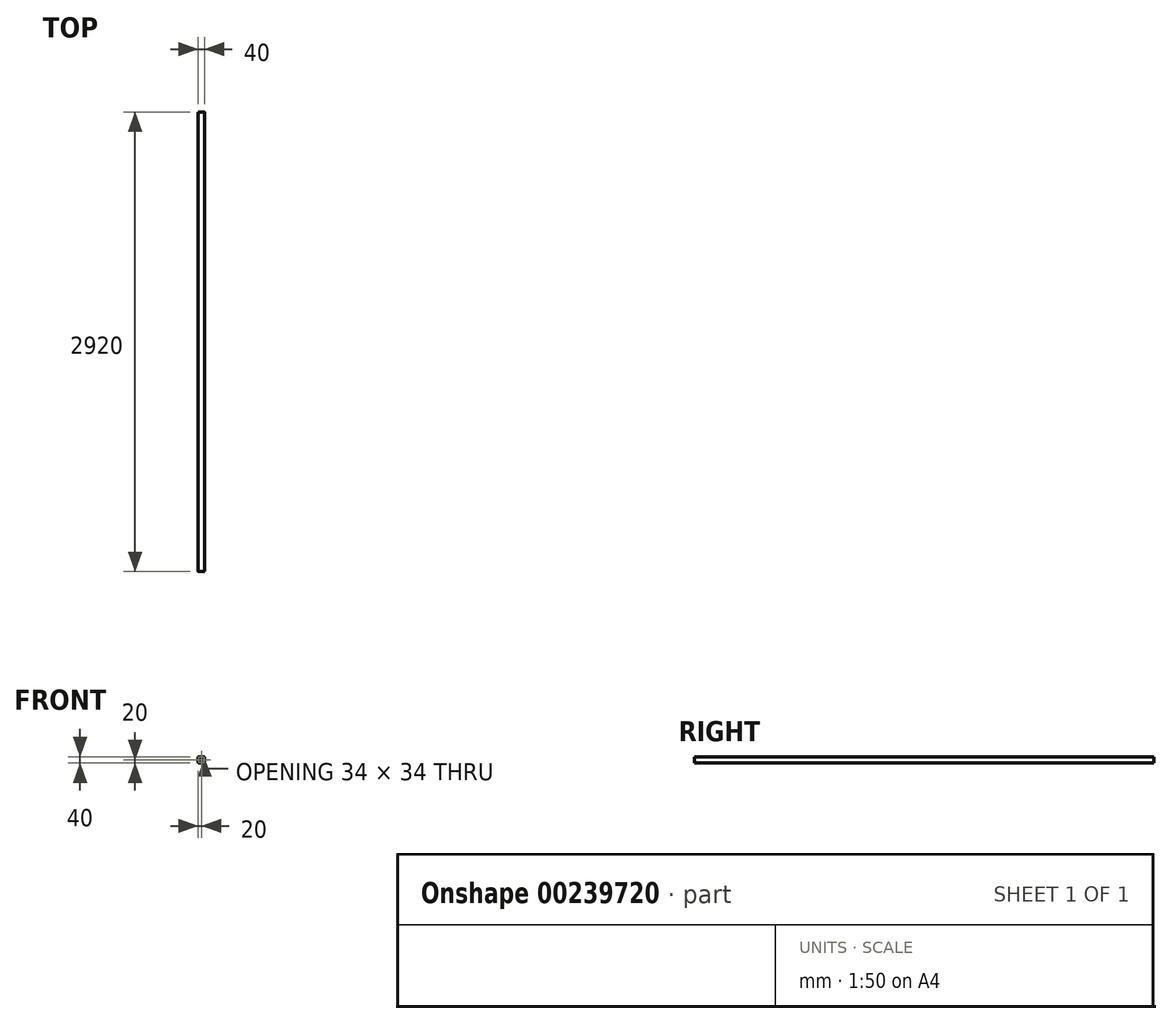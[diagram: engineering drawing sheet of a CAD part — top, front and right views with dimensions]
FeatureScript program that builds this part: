
annotation { "Feature Type Name" : "Feature", "Feature Type Description" : "" }
export const myFeature = defineFeature(function(context is Context, id is Id, definition is map)
    precondition{}
    {
        {
            var Q0;
            Q0=qCreatedBy(makeId("Front.planeOp"),FACE);
            var sketch = newSketch(context, id + "F0", { "sketchPlane" : qUnion([Q0])});
            skLineSegment(sketch, "E0.bottom", {"start": v(16, 20) * mm, "end": v(-16, 20) * mm});
            skLineSegment(sketch, "E0.top", {"start": v(16, -20) * mm, "end": v(-16, -20) * mm});
            skLineSegment(sketch, "E0.left", {"start": v(20, 16) * mm, "end": v(20, -16) * mm});
            skLineSegment(sketch, "E0.right", {"start": v(-20, 16) * mm, "end": v(-20, -16) * mm});
            skPoint(sketch, "E0.middle", {"position": v(0, 0) * mm});
            skPoint(sketch, "E1.visualSharp", {"position": v(-20, 20) * mm});
            skArc(sketch, "E1.filletArc", {"start": v(-16, 20) * mm, "mid": v(-18.83, 18.83) * mm, "end": v(-20, 16) * mm});
            skPoint(sketch, "E2.visualSharp", {"position": v(20, 20) * mm});
            skArc(sketch, "E2.filletArc", {"start": v(20, 16) * mm, "mid": v(18.83, 18.83) * mm, "end": v(16, 20) * mm});
            skPoint(sketch, "E3.visualSharp", {"position": v(20, -20) * mm});
            skArc(sketch, "E3.filletArc", {"start": v(16, -20) * mm, "mid": v(18.83, -18.83) * mm, "end": v(20, -16) * mm});
            skPoint(sketch, "E4.visualSharp", {"position": v(-20, -20) * mm});
            skArc(sketch, "E4.filletArc", {"start": v(-20, -16) * mm, "mid": v(-18.83, -18.83) * mm, "end": v(-16, -20) * mm});
            skLineSegment(sketch, "E5.0", {"start": v(16, 17) * mm, "end": v(-16, 17) * mm});
            skArc(sketch, "E5.1", {"start": v(17, 16) * mm, "mid": v(16.7, 16.7) * mm, "end": v(16, 17) * mm});
            skArc(sketch, "E5.2", {"start": v(-16, 17) * mm, "mid": v(-16.7, 16.7) * mm, "end": v(-17, 16) * mm});
            skLineSegment(sketch, "E5.3", {"start": v(17, 16) * mm, "end": v(17, -16) * mm});
            skLineSegment(sketch, "E5.4", {"start": v(-17, 16) * mm, "end": v(-17, -16) * mm});
            skArc(sketch, "E5.5", {"start": v(-17, -16) * mm, "mid": v(-16.7, -16.7) * mm, "end": v(-16, -17) * mm});
            skLineSegment(sketch, "E5.6", {"start": v(16, -17) * mm, "end": v(-16, -17) * mm});
            skArc(sketch, "E5.7", {"start": v(16, -17) * mm, "mid": v(16.7, -16.7) * mm, "end": v(17, -16) * mm});
            skSolve(sketch);
        }
        {
            var Q0;
            Q0=makeQuery(id+"F0.imprint","IMPRINT",FACE,{"disambiguationData":[TD([[makeQuery(id+"F0.imprint","IMPRINT",EDGE,{"derivedFrom":sQuery(id+"F0.wireOp",EDGE,"E0.bottom")}),1.0]])]});
            extrude(context, id + "F1", {"entities" : qUnion([Q0]), "depth" : 2920 * mm});
        }
    });
